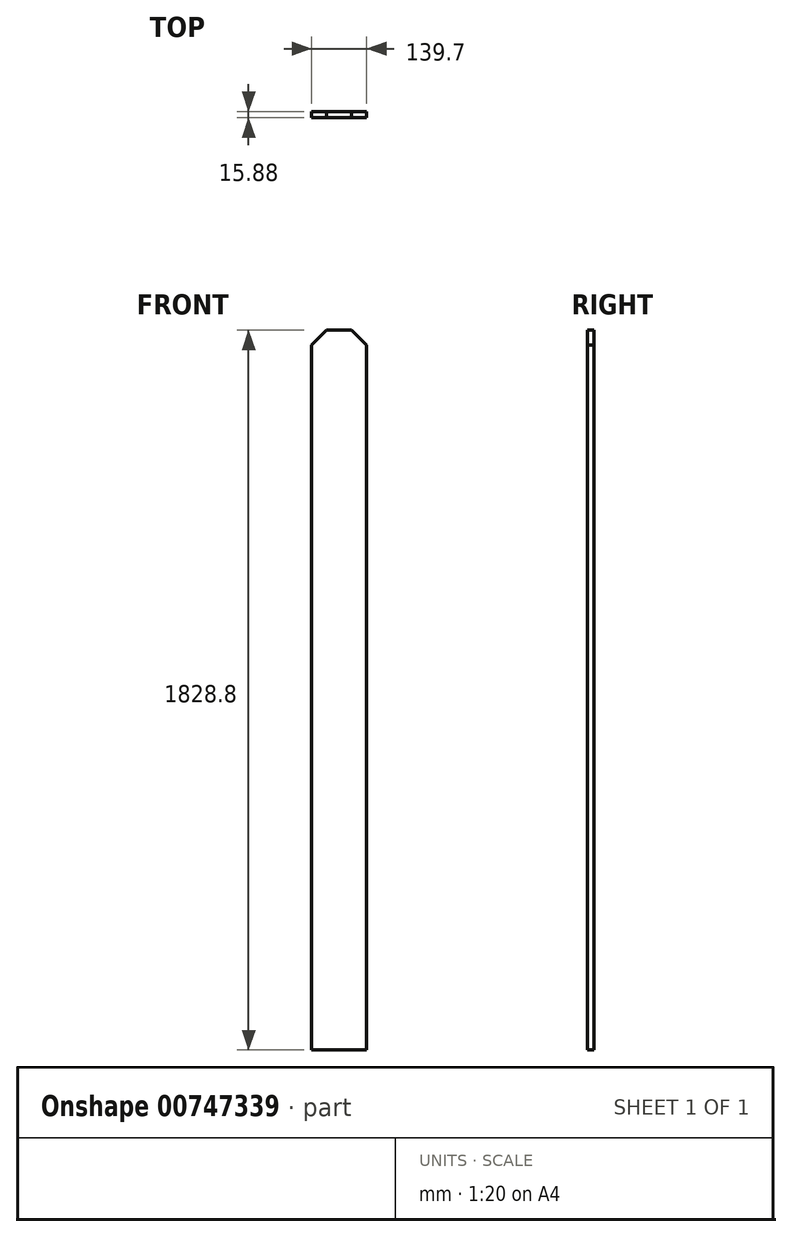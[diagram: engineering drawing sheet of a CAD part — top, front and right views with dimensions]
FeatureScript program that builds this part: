
annotation { "Feature Type Name" : "Feature", "Feature Type Description" : "" }
export const myFeature = defineFeature(function(context is Context, id is Id, definition is map)
    precondition{}
    {
        {
            var Q0;
            Q0=qCreatedBy(makeId("Front.planeOp"),FACE);
            var sketch = newSketch(context, id + "F0", { "sketchPlane" : qUnion([Q0])});
            skLineSegment(sketch, "E0.bottom", {"start": v(0, 0) * mm, "end": v(139.7, 0) * mm});
            skLineSegment(sketch, "E0.top", {"start": v(0, 1828.8) * mm, "end": v(139.7, 1828.8) * mm});
            skLineSegment(sketch, "E0.left", {"start": v(0, 0) * mm, "end": v(0, 1828.8) * mm});
            skLineSegment(sketch, "E0.right", {"start": v(139.7, 0) * mm, "end": v(139.7, 1828.8) * mm});
            skSolve(sketch);
        }
        {
            var Q0;
            Q0=makeQuery(id+"F0.imprint","IMPRINT",FACE,{"disambiguationData":[TD([[makeQuery(id+"F0.imprint","IMPRINT",EDGE,{"derivedFrom":sQuery(id+"F0.wireOp",EDGE,"E0.bottom")}),1.0]])]});
            extrude(context, id + "F1", {"entities" : qUnion([Q0]), "depth" : 15.88 * mm, "offsetDistance" : 25.4 * mm});
        }
        {
            var Q0;
            Q0=makeQuery(id+"F1.opExtrude","SWEPT_EDGE",EDGE,{"disambiguationData":[OSD([sQuery(id+"F0.wireOp",EDGE,"E0.top"),sQuery(id+"F0.wireOp",EDGE,"E0.left")])]});
            var Q1;
            Q1=makeQuery(id+"F1.opExtrude","SWEPT_EDGE",EDGE,{"disambiguationData":[OSD([sQuery(id+"F0.wireOp",EDGE,"E0.top"),sQuery(id+"F0.wireOp",EDGE,"E0.right")])]});
            chamfer(context, id + "F2", {"entities" : qUnion([Q0, Q1]), "width" : 38.1 * mm, "tangentPropagation" : true});
        }
    });
